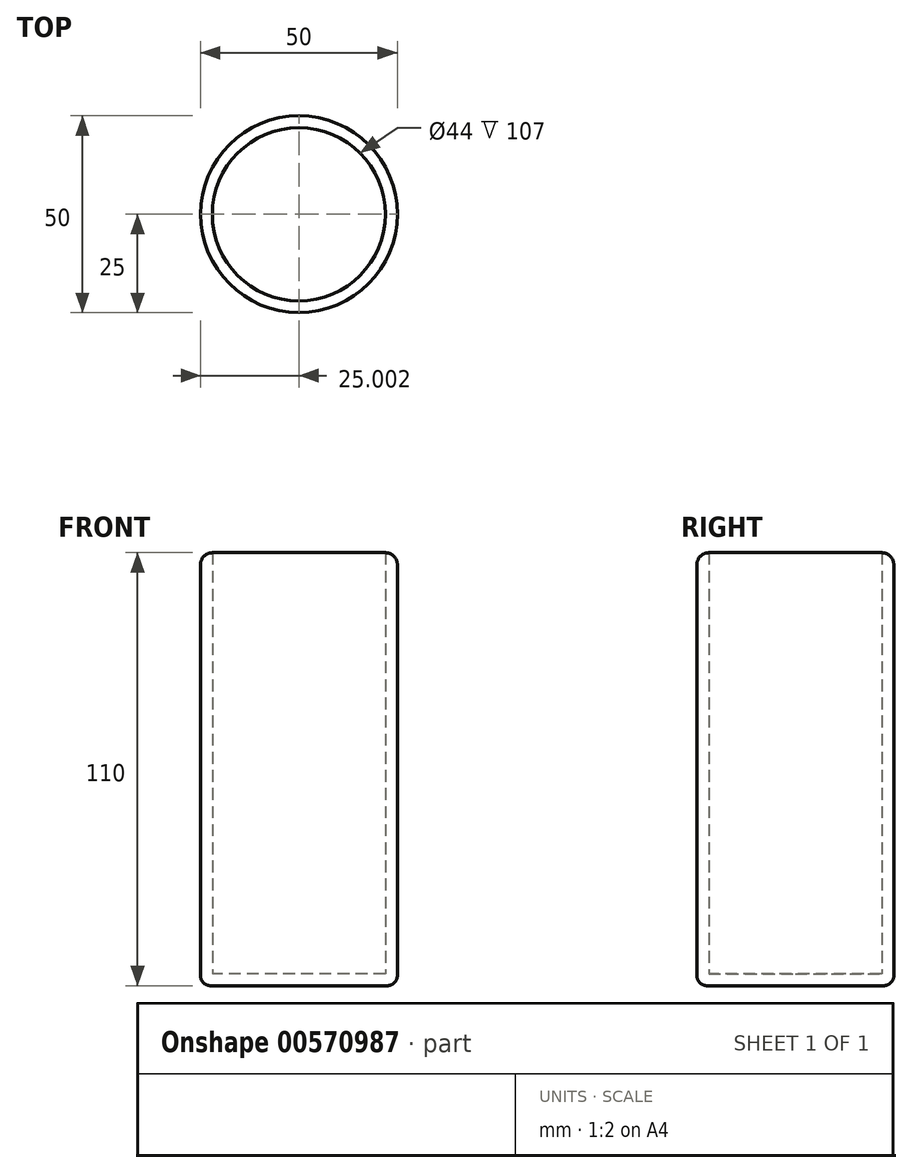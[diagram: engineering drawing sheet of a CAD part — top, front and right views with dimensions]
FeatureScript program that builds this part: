
annotation { "Feature Type Name" : "Feature", "Feature Type Description" : "" }
export const myFeature = defineFeature(function(context is Context, id is Id, definition is map)
    precondition{}
    {
        {
            var Q0;
            Q0=qCreatedBy(makeId("Top.planeOp"),FACE);
            var sketch = newSketch(context, id + "F0", { "sketchPlane" : qUnion([Q0])});
            skCircle(sketch, "E0", {"center": v(-6.16, 2.96) * mm, "radius": 25 * mm});
            skSolve(sketch);
        }
        {
            var Q0;
            Q0=makeQuery(id+"F0.imprint","IMPRINT",FACE,{"disambiguationData":[TD([[makeQuery(id+"F0.imprint","IMPRINT",EDGE,{"derivedFrom":sQuery(id+"F0.wireOp",EDGE,"E0")}),1.0]])]});
            extrude(context, id + "F1", {"entities" : qUnion([Q0]), "depth" : 110 * mm, "offsetDistance" : 25 * mm});
        }
        {
            var Q0;
            Q0=makeQuery(id+"F1.opExtrude","CAP_EDGE",EDGE,{"disambiguationData":[OSD([sQuery(id+"F0.wireOp",EDGE,"E0")])],"isStart":false});
            fillet(context, id + "F2", {"entities" : qUnion([Q0]), "radius" : 3 * mm, "tangentPropagation" : true, "allowEdgeOverflow" : false});
        }
        {
            var Q0;
            Q0=makeQuery(id+"F1.opExtrude","CAP_FACE",FACE,{"disambiguationData":[OSD([sQuery(id+"F0.wireOp",EDGE,"E0")])],"isStart":false});
            shell(context, id + "F3", {"entities" : qUnion([Q0]), "thickness" : 3 * mm});
        }
        {
            var Q0;
            Q0=makeQuery(id+"F1.opExtrude","CAP_EDGE",EDGE,{"disambiguationData":[OSD([sQuery(id+"F0.wireOp",EDGE,"E0")])],"isStart":true});
            fillet(context, id + "F4", {"entities" : qUnion([Q0]), "radius" : 2.5 * mm, "tangentPropagation" : true, "allowEdgeOverflow" : false});
        }
    });
